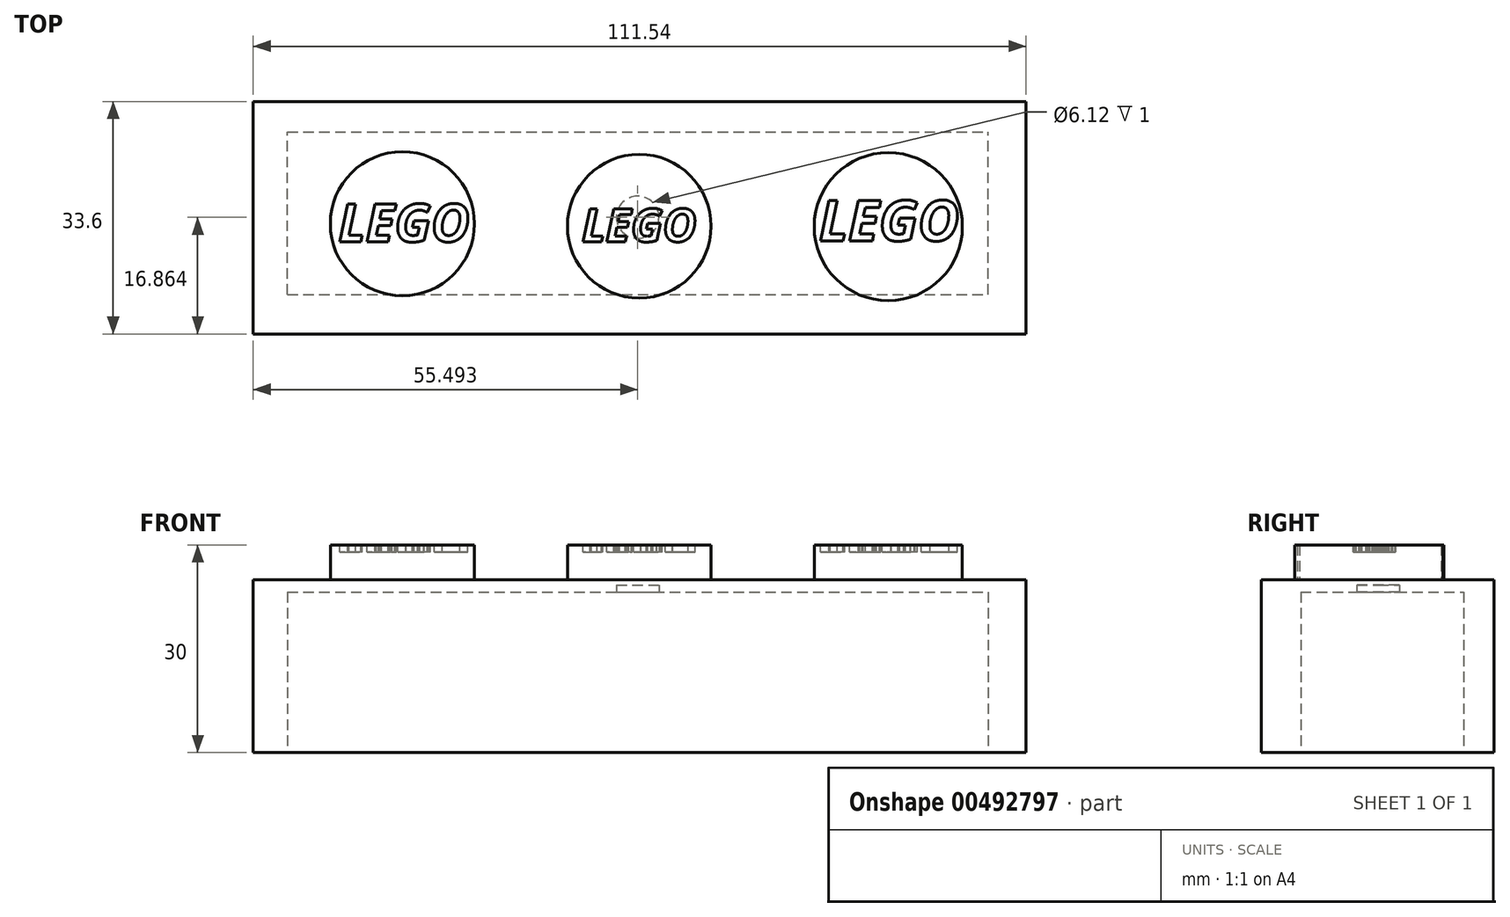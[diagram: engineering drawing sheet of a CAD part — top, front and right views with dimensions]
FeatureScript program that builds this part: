
annotation { "Feature Type Name" : "Feature", "Feature Type Description" : "" }
export const myFeature = defineFeature(function(context is Context, id is Id, definition is map)
    precondition{}
    {
        {
            var Q0;
            Q0=qCreatedBy(makeId("Top.planeOp"),FACE);
            var sketch = newSketch(context, id + "F0", { "sketchPlane" : qUnion([Q0])});
            skLineSegment(sketch, "E0.bottom", {"start": v(-98.7, 26.44) * mm, "end": v(12.85, 26.44) * mm});
            skLineSegment(sketch, "E0.top", {"start": v(-98.7, -7.16) * mm, "end": v(12.85, -7.16) * mm});
            skLineSegment(sketch, "E0.left", {"start": v(-98.7, 26.44) * mm, "end": v(-98.7, -7.16) * mm});
            skLineSegment(sketch, "E0.right", {"start": v(12.85, 26.44) * mm, "end": v(12.85, -7.16) * mm});
            skSolve(sketch);
        }
        {
            var Q0;
            Q0=makeQuery(id+"F0.imprint","IMPRINT",FACE,{"disambiguationData":[TD([[makeQuery(id+"F0.imprint","IMPRINT",EDGE,{"derivedFrom":sQuery(id+"F0.wireOp",EDGE,"E0.bottom")}),-1.0]])]});
            extrude(context, id + "F1", {"entities" : qUnion([Q0]), "depth" : 25 * mm});
        }
        {
            var Q0;
            Q0=makeQuery(id+"F1.opExtrude","CAP_FACE",FACE,{"disambiguationData":[OSD([sQuery(id+"F0.wireOp",EDGE,"E0.bottom"),sQuery(id+"F0.wireOp",EDGE,"E0.top"),sQuery(id+"F0.wireOp",EDGE,"E0.left"),sQuery(id+"F0.wireOp",EDGE,"E0.right")])],"isStart":false});
            var sketch = newSketch(context, id + "F2", { "sketchPlane" : qUnion([Q0])});
            skCircle(sketch, "E1", {"center": v(-77.16, 8.77) * mm, "radius": 10.4 * mm});
            skSolve(sketch);
        }
        {
            var Q0;
            Q0 = qSketchRegion(id + "F2", true);
            extrude(context, id + "F3", {"entities" : qUnion([Q0]), "operationType" : NewBodyOperationType.ADD, "depth" : 5 * mm});
        }
        {
            var Q0;
            Q0=makeQuery(id+"F3.opExtrude","CAP_FACE",FACE,{"disambiguationData":[OSD([sQuery(id+"F2.wireOp",EDGE,"E1")])],"isStart":false});
            var sketch = newSketch(context, id + "F4", { "sketchPlane" : qUnion([Q0])});
            skText(sketch, "E2", { "text": "LEGO", "fontName": "OpenSans-BoldItalic.ttf"});
            const initialGuessF4  = {"E2": [-0.08641, 0.00617, 1, 0, 0.0055]};
            skSetInitialGuess(sketch, initialGuessF4);
            skSolve(sketch);
        }
        {
            var Q0;
            Q0 = qSketchRegion(id + "F4", true);
            extrude(context, id + "F5", {"entities" : qUnion([Q0]), "operationType" : NewBodyOperationType.REMOVE, "oppositeDirection" : true, "depth" : 1 * mm});
        }
        {
            var Q0;
            Q0=makeQuery(id+"F1.opExtrude","CAP_FACE",FACE,{"disambiguationData":[OSD([sQuery(id+"F0.wireOp",EDGE,"E0.bottom"),sQuery(id+"F0.wireOp",EDGE,"E0.top"),sQuery(id+"F0.wireOp",EDGE,"E0.left"),sQuery(id+"F0.wireOp",EDGE,"E0.right")])],"isStart":true});
            var sketch = newSketch(context, id + "F6", { "sketchPlane" : qUnion([Q0])});
            skLineSegment(sketch, "E3.bottom", {"start": v(-93.77, 1.46) * mm, "end": v(7.37, 1.46) * mm});
            skLineSegment(sketch, "E3.top", {"start": v(-93.77, -22.02) * mm, "end": v(7.37, -22.02) * mm});
            skLineSegment(sketch, "E3.left", {"start": v(-93.77, 1.46) * mm, "end": v(-93.77, -22.02) * mm});
            skLineSegment(sketch, "E3.right", {"start": v(7.37, 1.46) * mm, "end": v(7.37, -22.02) * mm});
            skSolve(sketch);
        }
        {
            var Q0;
            Q0 = qSketchRegion(id + "F6", true);
            extrude(context, id + "F7", {"entities" : qUnion([Q0]), "operationType" : NewBodyOperationType.REMOVE, "oppositeDirection" : true, "depth" : 23.2 * mm});
        }
        {
            var Q0;
            Q0=makeQuery(id+"F1.opExtrude","CAP_FACE",FACE,{"disambiguationData":[OSD([sQuery(id+"F0.wireOp",EDGE,"E0.bottom"),sQuery(id+"F0.wireOp",EDGE,"E0.top"),sQuery(id+"F0.wireOp",EDGE,"E0.left"),sQuery(id+"F0.wireOp",EDGE,"E0.right")])],"isStart":false});
            var sketch = newSketch(context, id + "F8", { "sketchPlane" : qUnion([Q0])});
            skCircle(sketch, "E4", {"center": v(-42.97, 8.41) * mm, "radius": 10.37 * mm});
            skCircle(sketch, "E5", {"center": v(-7.02, 8.36) * mm, "radius": 10.7 * mm});
            skSolve(sketch);
        }
        {
            var Q0;
            Q0=makeQuery(id+"F8.imprint","IMPRINT",FACE,{"disambiguationData":[TD([[makeQuery(id+"F8.imprint","IMPRINT",EDGE,{"derivedFrom":sQuery(id+"F8.wireOp",EDGE,"E4")}),1.0]])]});
            var Q1;
            Q1=makeQuery(id+"F8.imprint","IMPRINT",FACE,{"disambiguationData":[TD([[makeQuery(id+"F8.imprint","IMPRINT",EDGE,{"derivedFrom":sQuery(id+"F8.wireOp",EDGE,"E5")}),1.0]])]});
            extrude(context, id + "F9", {"entities" : qUnion([Q0, Q1]), "operationType" : NewBodyOperationType.ADD, "depth" : 5 * mm});
        }
        {
            var Q0;
            Q0=makeQuery(id+"F9.opExtrude","CAP_FACE",FACE,{"disambiguationData":[OSD([sQuery(id+"F8.wireOp",EDGE,"E4")])],"isStart":false});
            var sketch = newSketch(context, id + "F10", { "sketchPlane" : qUnion([Q0])});
            skText(sketch, "E6", { "text": "LEGO", "fontName": "OpenSans-BoldItalic.ttf"});
            const initialGuessF10  = {"E6": [-0.05126, 0.00617, 1, 0, 0.0048]};
            skSetInitialGuess(sketch, initialGuessF10);
            skSolve(sketch);
        }
        {
            var Q0;
            Q0 = qSketchRegion(id + "F10", true);
            extrude(context, id + "F11", {"entities" : qUnion([Q0]), "operationType" : NewBodyOperationType.REMOVE, "oppositeDirection" : true, "depth" : 1 * mm});
        }
        {
            var Q0;
            Q0=makeQuery(id+"F9.opExtrude","CAP_FACE",FACE,{"disambiguationData":[OSD([sQuery(id+"F8.wireOp",EDGE,"E5")])],"isStart":false});
            var sketch = newSketch(context, id + "F12", { "sketchPlane" : qUnion([Q0])});
            skText(sketch, "E7", { "text": "LEGO", "fontName": "OpenSans-BoldItalic.ttf"});
            const initialGuessF12  = {"E7": [-0.01702, 0.0063, 1, 0, 0.00587]};
            skSetInitialGuess(sketch, initialGuessF12);
            skSolve(sketch);
        }
        {
            var Q0;
            Q0 = qSketchRegion(id + "F12", true);
            extrude(context, id + "F13", {"entities" : qUnion([Q0]), "operationType" : NewBodyOperationType.REMOVE, "oppositeDirection" : true, "depth" : 1 * mm});
        }
        {
            var Q0;
            Q0=makeQuery(id+"F7.boolean.opBoolean","COPY",FACE,{"derivedFrom":makeQuery(id+"F7.opExtrude","CAP_FACE",FACE,{"disambiguationData":[OSD([sQuery(id+"F6.wireOp",EDGE,"E3.bottom"),sQuery(id+"F6.wireOp",EDGE,"E3.top"),sQuery(id+"F6.wireOp",EDGE,"E3.left"),sQuery(id+"F6.wireOp",EDGE,"E3.right")])],"isStart":false})});
            var sketch = newSketch(context, id + "F14", { "sketchPlane" : qUnion([Q0])});
            skCircle(sketch, "E8", {"center": v(-43.2, -9.7) * mm, "radius": 3.06 * mm});
            skSolve(sketch);
        }
        {
            var Q0;
            Q0 = qSketchRegion(id + "F14", true);
            extrude(context, id + "F15", {"entities" : qUnion([Q0]), "operationType" : NewBodyOperationType.REMOVE, "oppositeDirection" : true, "depth" : 1 * mm});
        }
    });
